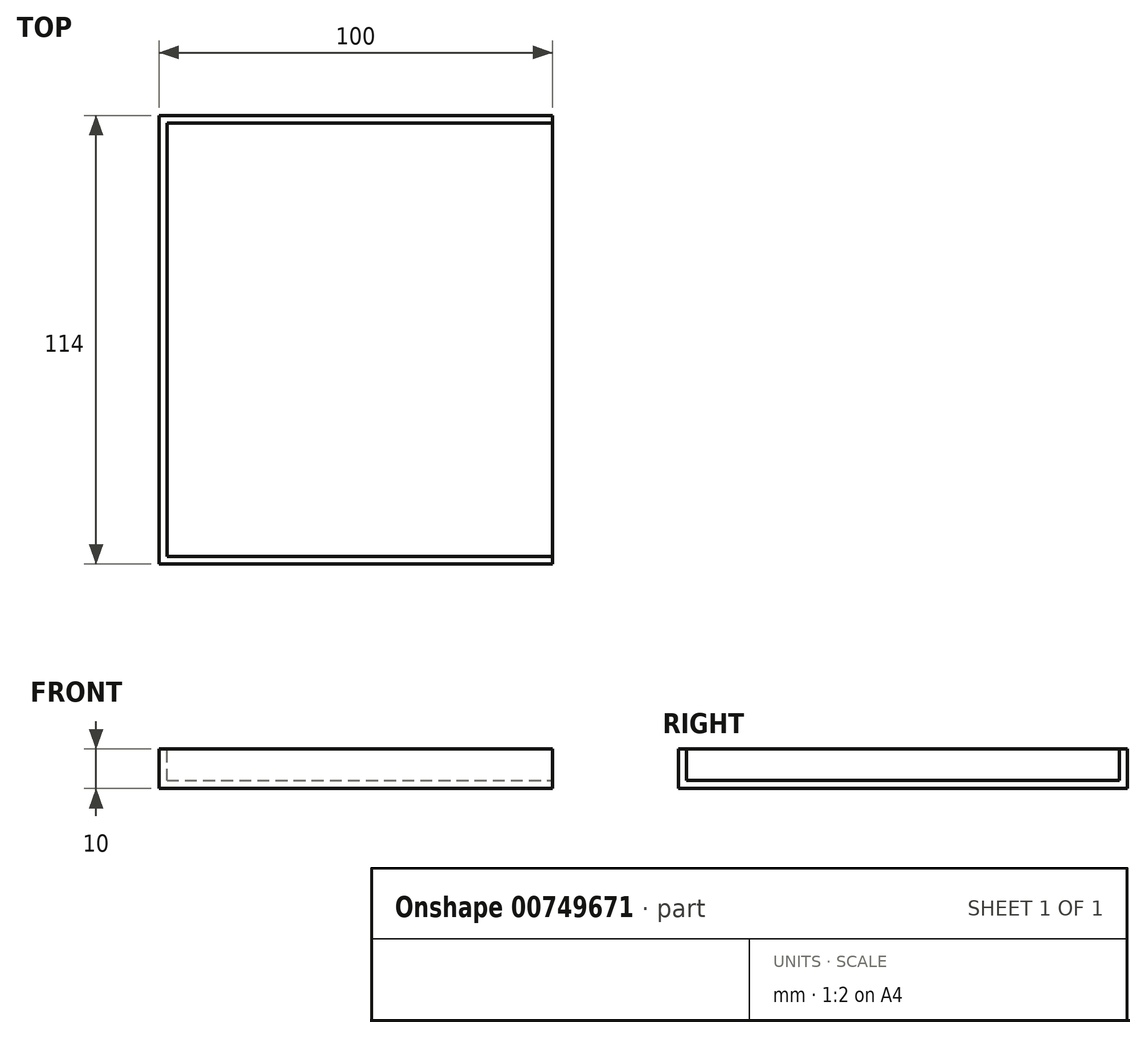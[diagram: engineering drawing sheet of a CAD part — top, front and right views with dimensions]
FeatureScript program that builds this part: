
annotation { "Feature Type Name" : "Feature", "Feature Type Description" : "" }
export const myFeature = defineFeature(function(context is Context, id is Id, definition is map)
    precondition{}
    {
        {
            var Q0;
            Q0=qCreatedBy(makeId("Top.planeOp"),FACE);
            var sketch = newSketch(context, id + "F0", { "sketchPlane" : qUnion([Q0])});
            skLineSegment(sketch, "E0.bottom", {"start": v(-89.45, 57) * mm, "end": v(10.55, 57) * mm});
            skLineSegment(sketch, "E0.top", {"start": v(-89.45, -57) * mm, "end": v(10.55, -57) * mm});
            skLineSegment(sketch, "E0.left", {"start": v(-89.45, 57) * mm, "end": v(-89.45, -57) * mm});
            skLineSegment(sketch, "E0.right", {"start": v(10.55, 57) * mm, "end": v(10.55, -57) * mm});
            skSolve(sketch);
        }
        {
            var Q0;
            Q0 = qSketchRegion(id + "F0", true);
            extrude(context, id + "F1", {"entities" : qUnion([Q0]), "depth" : 10 * mm, "offsetDistance" : 25 * mm});
        }
        {
            var Q0;
            Q0=makeQuery(id+"F1.opExtrude","CAP_FACE",FACE,{"disambiguationData":[OSD([sQuery(id+"F0.wireOp",EDGE,"E0.bottom"),sQuery(id+"F0.wireOp",EDGE,"E0.top"),sQuery(id+"F0.wireOp",EDGE,"E0.left"),sQuery(id+"F0.wireOp",EDGE,"E0.right")])],"isStart":false});
            var sketch = newSketch(context, id + "F2", { "sketchPlane" : qUnion([Q0])});
            skLineSegment(sketch, "E1.0", {"start": v(-89.45, 57) * mm, "end": v(10.55, 57) * mm, "construction": true});
            skLineSegment(sketch, "E1.1", {"start": v(-89.45, 57) * mm, "end": v(-89.45, -57) * mm, "construction": true});
            skLineSegment(sketch, "E1.2", {"start": v(10.55, 57) * mm, "end": v(10.55, -57) * mm, "construction": true});
            skLineSegment(sketch, "E1.3", {"start": v(-89.45, -57) * mm, "end": v(10.55, -57) * mm, "construction": true});
            skLineSegment(sketch, "E2.bottom", {"start": v(-87.45, 55) * mm, "end": v(15.93, 55) * mm});
            skLineSegment(sketch, "E2.top", {"start": v(-87.45, -55) * mm, "end": v(15.93, -55) * mm});
            skLineSegment(sketch, "E2.left", {"start": v(-87.45, 55) * mm, "end": v(-87.45, -55) * mm});
            skLineSegment(sketch, "E2.right", {"start": v(15.93, 55) * mm, "end": v(15.93, -55) * mm});
            skSolve(sketch);
        }
        {
            var Q0;
            Q0 = qSketchRegion(id + "F2", true);
            extrude(context, id + "F3", {"entities" : qUnion([Q0]), "operationType" : NewBodyOperationType.REMOVE, "oppositeDirection" : true, "depth" : 8 * mm, "offsetDistance" : 25 * mm});
        }
    });
